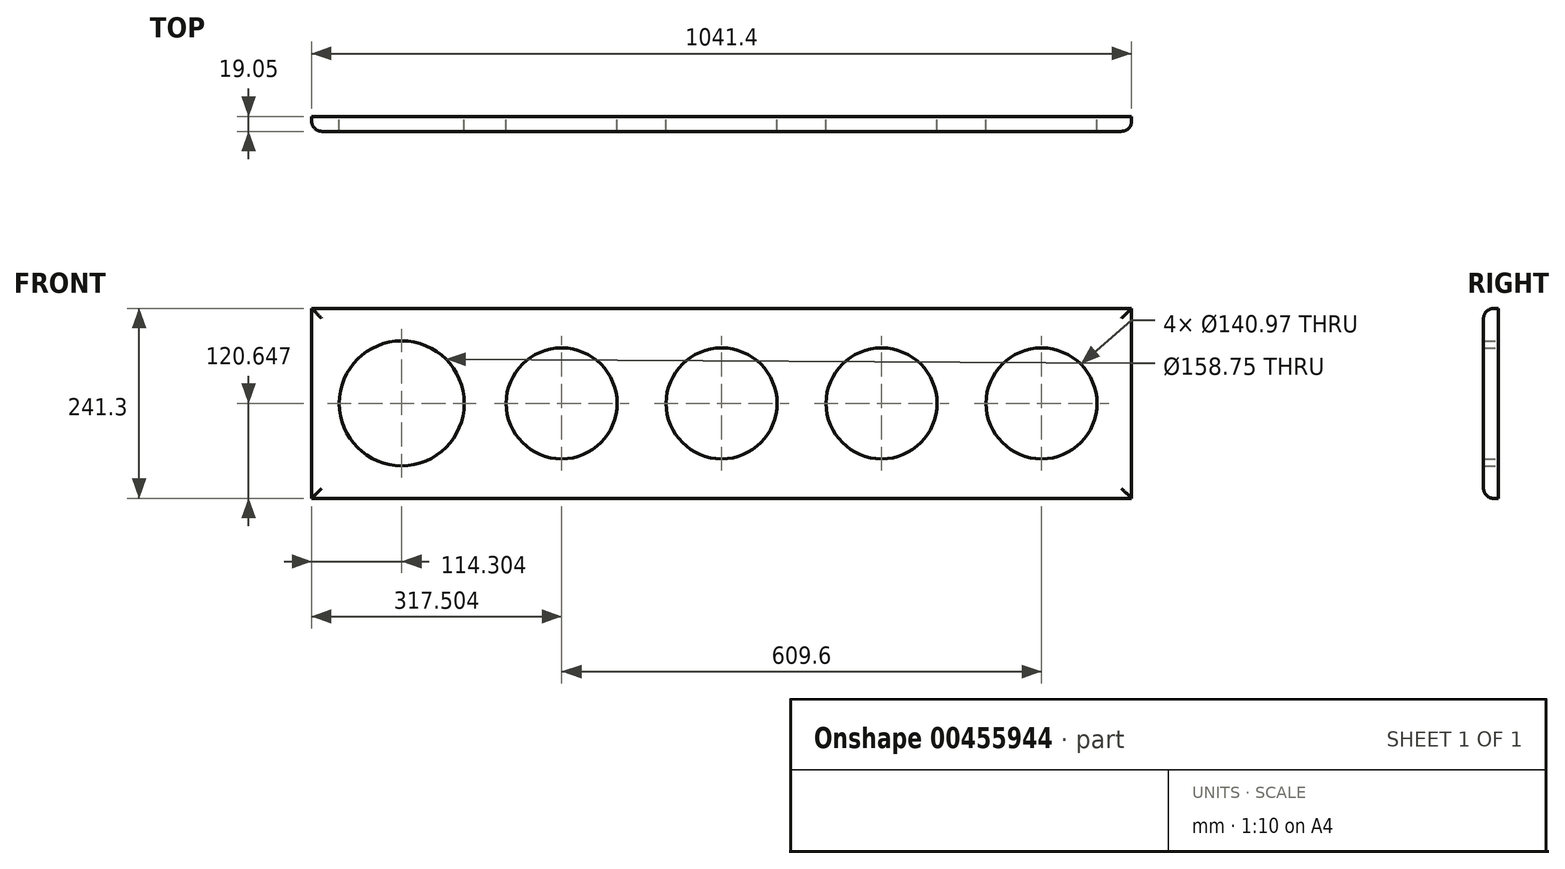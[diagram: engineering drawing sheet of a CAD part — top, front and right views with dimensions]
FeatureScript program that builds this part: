
annotation { "Feature Type Name" : "Feature", "Feature Type Description" : "" }
export const myFeature = defineFeature(function(context is Context, id is Id, definition is map)
    precondition{}
    {
        {
            var Q0;
            Q0=qCreatedBy(makeId("Front.planeOp"),FACE);
            var sketch = newSketch(context, id + "F0", { "sketchPlane" : qUnion([Q0])});
            skLineSegment(sketch, "E0.bottom", {"start": v(-502.9, 2.2) * mm, "end": v(538.5, 2.2) * mm});
            skLineSegment(sketch, "E0.top", {"start": v(-502.9, -239.1) * mm, "end": v(538.5, -239.1) * mm});
            skLineSegment(sketch, "E0.left", {"start": v(-502.9, 2.2) * mm, "end": v(-502.9, -239.1) * mm});
            skLineSegment(sketch, "E0.right", {"start": v(538.5, 2.2) * mm, "end": v(538.5, -239.1) * mm});
            skLineSegment(sketch, "E1", {"start": v(-388.6, -118.44) * mm, "end": v(-185.4, -118.44) * mm, "construction": true});
            skLineSegment(sketch, "E2", {"start": v(-185.4, -118.44) * mm, "end": v(17.8, -118.44) * mm, "construction": true});
            skLineSegment(sketch, "E3", {"start": v(17.8, -118.44) * mm, "end": v(221, -118.44) * mm, "construction": true});
            skLineSegment(sketch, "E4", {"start": v(221, -118.44) * mm, "end": v(424.2, -118.44) * mm, "construction": true});
            skCircle(sketch, "E5", {"center": v(-185.4, -118.44) * mm, "radius": 70.48 * mm});
            skCircle(sketch, "E6", {"center": v(17.8, -118.44) * mm, "radius": 70.48 * mm});
            skCircle(sketch, "E7", {"center": v(221, -118.44) * mm, "radius": 70.48 * mm});
            skCircle(sketch, "E8", {"center": v(424.2, -118.44) * mm, "radius": 70.48 * mm});
            skCircle(sketch, "E9", {"center": v(-388.6, -118.44) * mm, "radius": 79.38 * mm});
            skLineSegment(sketch, "E10", {"start": v(424.2, -118.44) * mm, "end": v(538.5, -118.44) * mm, "construction": true});
            skSolve(sketch);
        }
        {
            var Q0;
            Q0=makeQuery(id+"F0.imprint","IMPRINT",FACE,{"disambiguationData":[TD([[makeQuery(id+"F0.imprint","IMPRINT",EDGE,{"derivedFrom":sQuery(id+"F0.wireOp",EDGE,"E0.bottom")}),-1.0]])]});
            extrude(context, id + "F1", {"entities" : qUnion([Q0]), "depth" : 19.05 * mm, "offsetDistance" : 25.4 * mm});
        }
        {
            var Q0;
            Q0=makeQuery(id+"F1.opExtrude","CAP_EDGE",EDGE,{"disambiguationData":[OSD([sQuery(id+"F0.wireOp",EDGE,"E0.bottom")])],"isStart":false});
            var Q1;
            Q1=makeQuery(id+"F1.opExtrude","CAP_EDGE",EDGE,{"disambiguationData":[OSD([sQuery(id+"F0.wireOp",EDGE,"E0.left")])],"isStart":false});
            var Q2;
            Q2=makeQuery(id+"F1.opExtrude","CAP_EDGE",EDGE,{"disambiguationData":[OSD([sQuery(id+"F0.wireOp",EDGE,"E0.top")])],"isStart":false});
            var Q3;
            Q3=makeQuery(id+"F1.opExtrude","CAP_EDGE",EDGE,{"disambiguationData":[OSD([sQuery(id+"F0.wireOp",EDGE,"E0.right")])],"isStart":false});
            fillet(context, id + "F2", {"entities" : qUnion([Q0, Q1, Q2, Q3]), "tangentPropagation" : true, "radius" : 12.7 * mm, "defaultsChanged" : true, "vertexSettings" : [], "allowEdgeOverflow" : false});
        }
    });
